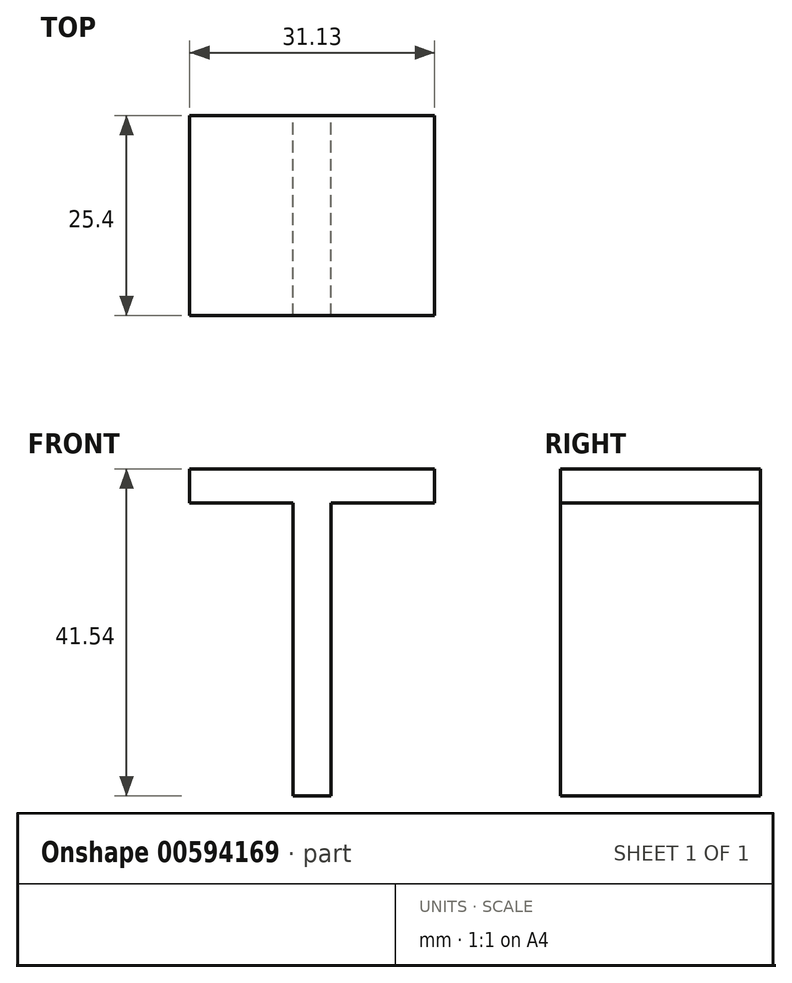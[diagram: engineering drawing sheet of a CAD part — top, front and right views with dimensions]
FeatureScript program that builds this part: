
annotation { "Feature Type Name" : "Feature", "Feature Type Description" : "" }
export const myFeature = defineFeature(function(context is Context, id is Id, definition is map)
    precondition{}
    {
        {
            var Q0;
            Q0=qCreatedBy(makeId("Front.planeOp"),FACE);
            var sketch = newSketch(context, id + "F0", { "sketchPlane" : qUnion([Q0])});
            skText(sketch, "E0", { "text": "T", "fontName": "OpenSans-Regular.ttf"});
            const initialGuessF0  = {"E0": [-0.03921, 0, 1, 0, 0.04189]};
            skSetInitialGuess(sketch, initialGuessF0);
            skSolve(sketch);
        }
        {
            var Q0;
            Q0 = qSketchRegion(id + "F0", true);
            extrude(context, id + "F1", {"entities" : qUnion([Q0]), "depth" : 25.4 * mm, "offsetDistance" : 25.4 * mm});
        }
    });
